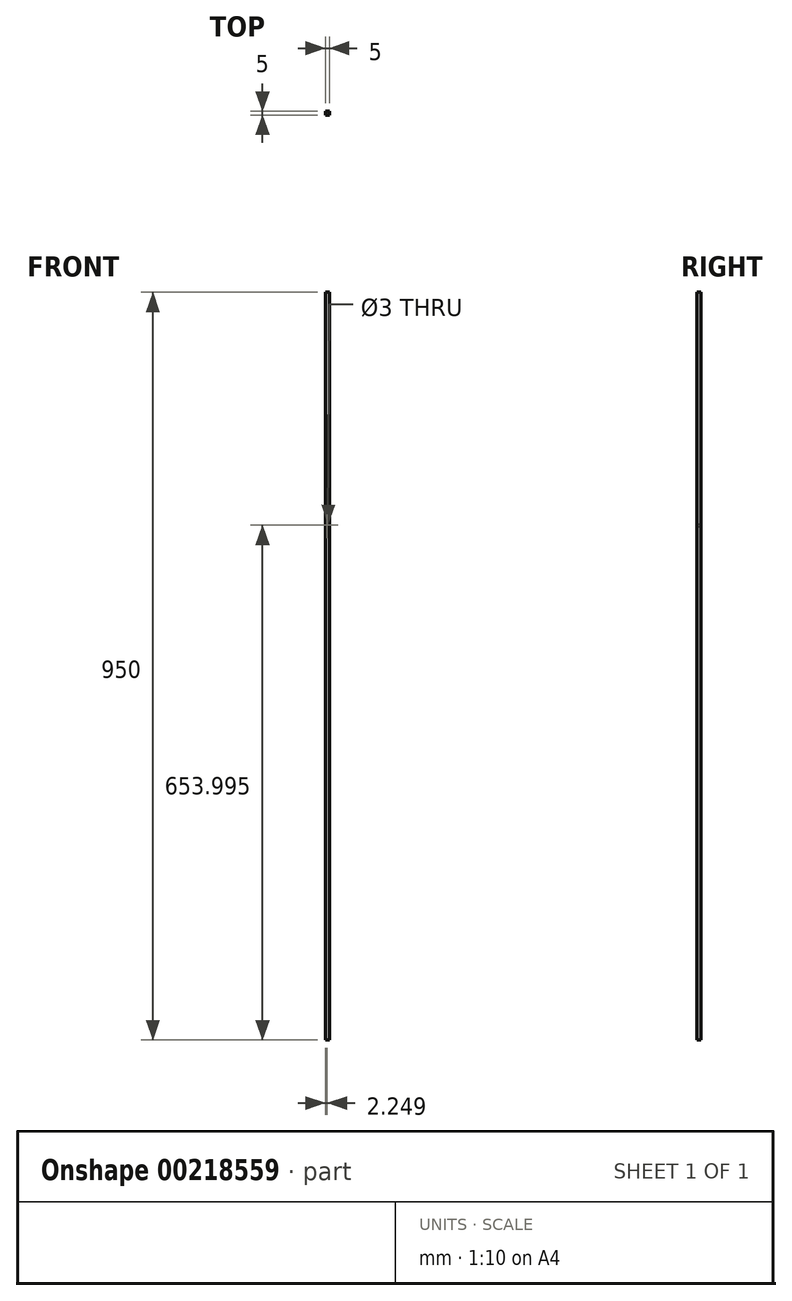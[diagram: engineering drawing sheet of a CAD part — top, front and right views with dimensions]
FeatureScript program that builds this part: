
annotation { "Feature Type Name" : "Feature", "Feature Type Description" : "" }
export const myFeature = defineFeature(function(context is Context, id is Id, definition is map)
    precondition{}
    {
        {
            var Q0;
            Q0=qCreatedBy(makeId("Front.planeOp"),FACE);
            var sketch = newSketch(context, id + "F0", { "sketchPlane" : qUnion([Q0])});
            skLineSegment(sketch, "E0", {"start": v(62.34, 12.72) * mm, "end": v(-131.55, 12.72) * mm, "construction": true});
            skLineSegment(sketch, "E1.bottom", {"start": v(-61.8, 983.67) * mm, "end": v(-56.8, 983.67) * mm});
            skLineSegment(sketch, "E1.top", {"start": v(-61.8, 33.67) * mm, "end": v(-56.8, 33.67) * mm});
            skLineSegment(sketch, "E1.left", {"start": v(-61.8, 983.67) * mm, "end": v(-61.8, 33.67) * mm});
            skLineSegment(sketch, "E1.right", {"start": v(-56.8, 983.67) * mm, "end": v(-56.8, 33.67) * mm});
            skCircle(sketch, "E2", {"center": v(-59.54, 687.67) * mm, "radius": 1.5 * mm});
            skSolve(sketch);
        }
        {
            var Q0;
            Q0=makeQuery(id+"F0.imprint","IMPRINT",FACE,{"disambiguationData":[TD([[makeQuery(id+"F0.imprint","IMPRINT",EDGE,{"derivedFrom":sQuery(id+"F0.wireOp",EDGE,"d1FpiweB-XVUe-nvXo-fNVb-qYOH3jzAyiQH")}),1.0]])]});
            var Q1;
            Q1=makeQuery(id+"F0.imprint","IMPRINT",FACE,{"disambiguationData":[TD([[makeQuery(id+"F0.imprint","IMPRINT",EDGE,{"derivedFrom":sQuery(id+"F0.wireOp",EDGE,"E1.bottom")}),-1.0]])]});
            extrude(context, id + "F1", {"entities" : qUnion([Q0, Q1]), "depth" : 5 * mm});
        }
    });
